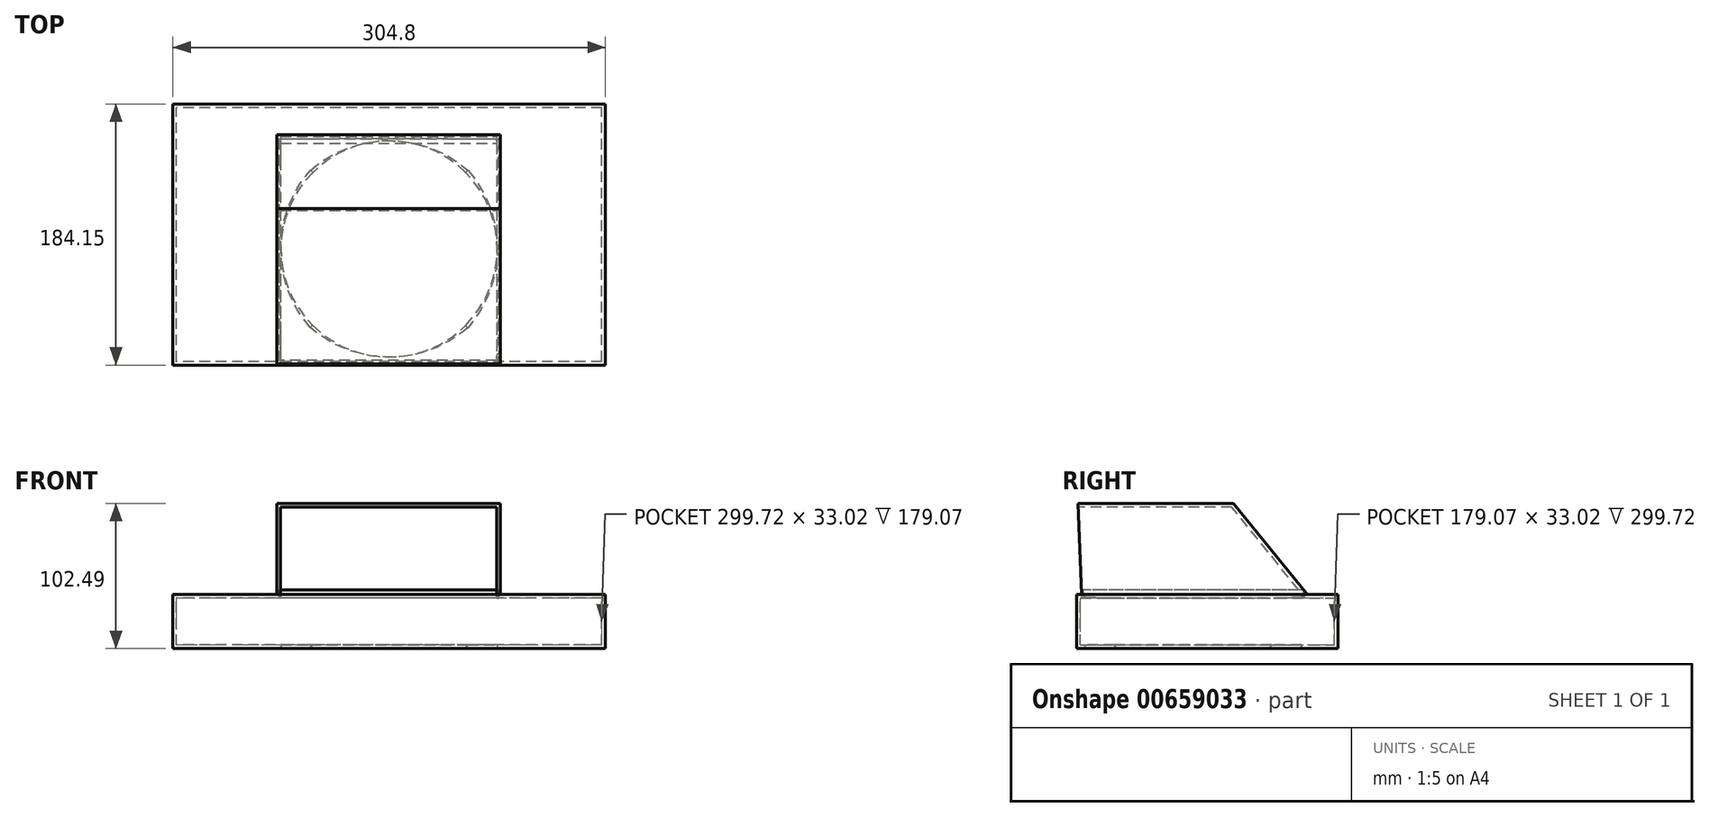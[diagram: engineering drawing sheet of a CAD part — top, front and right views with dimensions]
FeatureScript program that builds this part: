
annotation { "Feature Type Name" : "Feature", "Feature Type Description" : "" }
export const myFeature = defineFeature(function(context is Context, id is Id, definition is map)
    precondition{}
    {
        {
            var Q0;
            Q0=qCreatedBy(makeId("Front.planeOp"),FACE);
            var sketch = newSketch(context, id + "F0", { "sketchPlane" : qUnion([Q0])});
            skLineSegment(sketch, "E0.bottom", {"start": v(0, 0) * mm, "end": v(-304.8, 0) * mm});
            skLineSegment(sketch, "E0.top", {"start": v(0, 38.1) * mm, "end": v(-304.8, 38.1) * mm});
            skLineSegment(sketch, "E0.left", {"start": v(0, 0) * mm, "end": v(0, 38.1) * mm});
            skLineSegment(sketch, "E0.right", {"start": v(-304.8, 0) * mm, "end": v(-304.8, 38.1) * mm});
            skSolve(sketch);
        }
        {
            var Q0;
            Q0=makeQuery(id+"F0.imprint","IMPRINT",FACE,{"disambiguationData":[TD([[makeQuery(id+"F0.imprint","IMPRINT",EDGE,{"derivedFrom":sQuery(id+"F0.wireOp",EDGE,"E0.bottom")}),-1.0]])]});
            extrude(context, id + "F1", {"entities" : qUnion([Q0]), "depth" : 184.15 * mm, "offsetDistance" : 25.4 * mm});
        }
        {
            var Q0;
            Q0=makeQuery(id+"F1.opExtrude","SWEPT_FACE",FACE,{"disambiguationData":[OSD([sQuery(id+"F0.wireOp",EDGE,"E0.bottom")])]});
            var sketch = newSketch(context, id + "F2", { "sketchPlane" : qUnion([Q0])});
            skLineSegment(sketch, "E1", {"start": v(-304.8, 25.4) * mm, "end": v(0, 25.4) * mm, "construction": true});
            skLineSegment(sketch, "E2", {"start": v(-152.4, 0) * mm, "end": v(-152.4, 184.15) * mm, "construction": true});
            skCircle(sketch, "E3", {"center": v(-152.4, 102.27) * mm, "radius": 76.2 * mm});
            skSolve(sketch);
        }
        {
            var Q0;
            Q0=makeQuery(id+"F1.opExtrude","SWEPT_FACE",FACE,{"disambiguationData":[OSD([sQuery(id+"F0.wireOp",EDGE,"E0.top")])]});
            var sketch = newSketch(context, id + "F3", { "sketchPlane" : qUnion([Q0])});
            skLineSegment(sketch, "E4.bottom", {"start": v(-229.83, -24.64) * mm, "end": v(-74.9, -24.64) * mm});
            skLineSegment(sketch, "E4.top", {"start": v(-229.83, -179.58) * mm, "end": v(-74.9, -179.58) * mm});
            skLineSegment(sketch, "E4.left", {"start": v(-229.83, -24.64) * mm, "end": v(-229.83, -179.58) * mm});
            skLineSegment(sketch, "E4.right", {"start": v(-74.9, -24.64) * mm, "end": v(-74.9, -179.58) * mm});
            skSolve(sketch);
        }
        {
            var Q0;
            Q0=qCreatedBy(makeId("Right.planeOp"),FACE);
            cPlane(context, id + "F4", {"entities" : qUnion([Q0]), "cplaneType" : CPlaneType.OFFSET, "offset" : 74.17 * mm, "oppositeDirection" : true, "width" : 152.4 * mm, "height" : 152.4 * mm});
        }
        {
            var Q0;
            Q0=qCreatedBy(id+"F4.planeOp",FACE);
            var sketch = newSketch(context, id + "F5", { "sketchPlane" : qUnion([Q0])});
            skLineSegment(sketch, "E5", {"start": v(-21.5, 37.62) * mm, "end": v(-73.75, 102.49) * mm});
            skLineSegment(sketch, "E6", {"start": v(-73.75, 102.49) * mm, "end": v(-183.47, 102.49) * mm});
            skLineSegment(sketch, "E7", {"start": v(-183.47, 102.49) * mm, "end": v(-180.77, 37.34) * mm});
            skLineSegment(sketch, "E8", {"start": v(-180.77, 37.34) * mm, "end": v(-21.5, 37.62) * mm});
            skSolve(sketch);
        }
        {
            var Q0;
            Q0=makeQuery(id+"F5.imprint","IMPRINT",FACE,{"disambiguationData":[TD([[makeQuery(id+"F5.imprint","IMPRINT",EDGE,{"derivedFrom":sQuery(id+"F5.wireOp",EDGE,"E5")}),1.0]])]});
            extrude(context, id + "F6", {"entities" : qUnion([Q0]), "operationType" : NewBodyOperationType.ADD, "oppositeDirection" : true, "depth" : 157.23 * mm, "offsetDistance" : 25.4 * mm});
        }
        {
            var Q0;
            Q0=makeQuery(id+"F6.opExtrude","SWEPT_FACE",FACE,{"disambiguationData":[OSD([sQuery(id+"F5.wireOp",EDGE,"E7")])]});
            shell(context, id + "F7", {"entities" : qUnion([Q0]), "thickness" : 2.54 * mm});
        }
        {
            var Q1;
            Q1=qSketchRegion(id+"F2",true);
            var Q2;
            Q2=qSketchRegion(id+"F3",true);
            loft(context, id + "F8", {"operationType" : NewBodyOperationType.REMOVE, "sheetProfilesArray" : [{ "sheetProfileEntities" : qUnion([Q1]) }, { "sheetProfileEntities" : qUnion([Q2]) }]});
        }
        {
            var Q0;
            Q0=qSketchRegion(id+"F3",true);
            extrude(context, id + "F9", {"entities" : qUnion([Q0]), "operationType" : NewBodyOperationType.REMOVE, "depth" : 3.25 * mm, "offsetDistance" : 25.4 * mm});
        }
        {
            var Q0;
            Q0=qSketchRegion(id+"F3",true);
            extrude(context, id + "F10", {"entities" : qUnion([Q0]), "operationType" : NewBodyOperationType.REMOVE, "depth" : 3.2 * mm, "offsetDistance" : 25.4 * mm});
        }
    });
